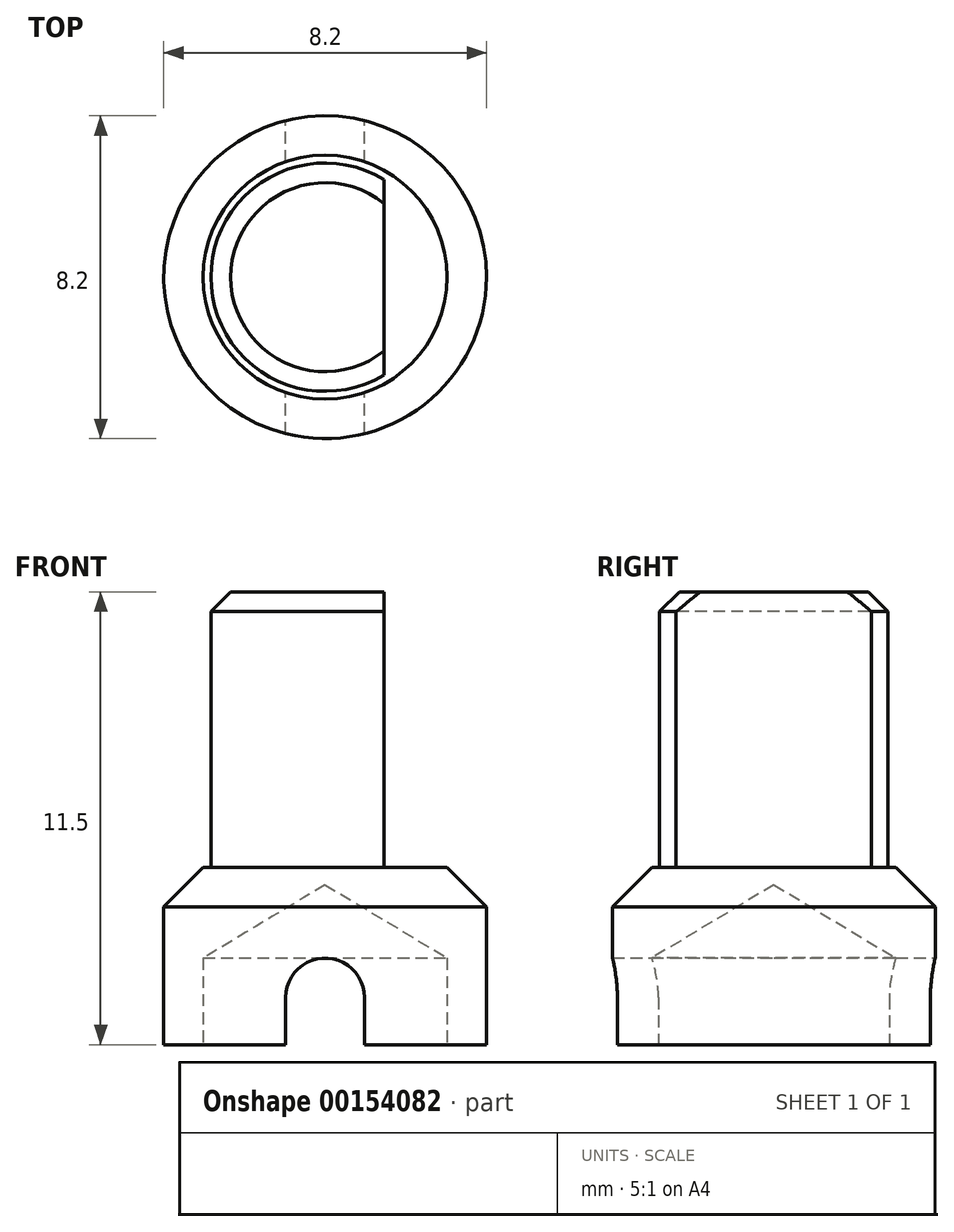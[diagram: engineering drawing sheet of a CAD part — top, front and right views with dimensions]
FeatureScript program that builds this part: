
annotation { "Feature Type Name" : "Feature", "Feature Type Description" : "" }
export const myFeature = defineFeature(function(context is Context, id is Id, definition is map)
    precondition{}
    {
        {
            var Q0;
            Q0=qCreatedBy(makeId("Top.planeOp"),FACE);
            var sketch = newSketch(context, id + "F0", { "sketchPlane" : qUnion([Q0])});
            skCircle(sketch, "E0", {"center": v(0, 0) * mm, "radius": 4.1 * mm});
            skSolve(sketch);
        }
        {
            var Q0;
            Q0=makeQuery(id+"F0.imprint","IMPRINT",FACE,{"disambiguationData":[TD([[makeQuery(id+"F0.imprint","IMPRINT",EDGE,{"derivedFrom":sQuery(id+"F0.wireOp",EDGE,"E0")}),1.0]])]});
            var Q1;
            Q1=sQuery(id+"F0.wireOp",EDGE,"E0");
            extrude(context, id + "F1", {"entities" : qUnion([Q0]), "surfaceEntities" : qUnion([Q1]), "depth" : 4.5 * mm});
        }
        {
            var Q0;
            Q0=sQuery(id+"F0.wireOp",VERTEX,"E0.center");
            var Q1;
            Q1=makeQuery(id+"F1.opExtrude","SWEPT_BODY",BODY,{"disambiguationData":[OSD([sQuery(id+"F0.wireOp",EDGE,"E0")])]});
            hole(context, id + "F2", {"style" : HoleStyle.SIMPLE, "endStyle" : HoleEndStyle.BLIND, "oppositeDirection" : true, "holeDiameter" : 6.2 * mm, "holeDepth" : 2.2 * mm, "locations" : qUnion([Q0]), "scope" : qUnion([Q1])});
        }
        {
            var Q0;
            Q0=makeQuery(id+"F1.opExtrude","CAP_FACE",FACE,{"disambiguationData":[OSD([sQuery(id+"F0.wireOp",EDGE,"E0")])],"isStart":false});
            var sketch = newSketch(context, id + "F3", { "sketchPlane" : qUnion([Q0])});
            skArc(sketch, "E1", {"start": v(1.5, 2.48) * mm, "mid": v(-2.9, 0) * mm, "end": v(1.5, -2.48) * mm});
            skLineSegment(sketch, "E2", {"start": v(1.5, 2.48) * mm, "end": v(1.5, -2.48) * mm});
            skSolve(sketch);
        }
        {
            var Q0;
            Q0=makeQuery(id+"F3.imprint","IMPRINT",FACE,{"disambiguationData":[TD([[makeQuery(id+"F3.imprint","IMPRINT",EDGE,{"derivedFrom":sQuery(id+"F3.wireOp",EDGE,"E1")}),1.0]])]});
            extrude(context, id + "F4", {"entities" : qUnion([Q0]), "operationType" : NewBodyOperationType.ADD, "depth" : 7 * mm});
        }
        {
            var Q0;
            Q0=makeQuery(id+"F4.opExtrude","CAP_EDGE",EDGE,{"disambiguationData":[OSD([sQuery(id+"F3.wireOp",EDGE,"E1")])],"isStart":false});
            chamfer(context, id + "F5", {"entities" : qUnion([Q0]), "width" : 0.5 * mm, "tangentPropagation" : true});
        }
        {
            var Q0;
            Q0=makeQuery(id+"F1.opExtrude","CAP_EDGE",EDGE,{"disambiguationData":[OSD([sQuery(id+"F0.wireOp",EDGE,"E0")])],"isStart":false});
            chamfer(context, id + "F6", {"entities" : qUnion([Q0]), "width" : 1 * mm, "tangentPropagation" : true});
        }
        {
            var Q0;
            Q0=qCreatedBy(makeId("Front.planeOp"),FACE);
            var sketch = newSketch(context, id + "F7", { "sketchPlane" : qUnion([Q0])});
            skLineSegment(sketch, "E3.bottom", {"start": v(-1, 0) * mm, "end": v(1, 0) * mm});
            skLineSegment(sketch, "E3.left", {"start": v(-1, 0) * mm, "end": v(-1, 1.2) * mm});
            skLineSegment(sketch, "E3.right", {"start": v(1, 0) * mm, "end": v(1, 1.2) * mm});
            skArc(sketch, "E4", {"start": v(-1, 1.2) * mm, "mid": v(0, 2.2) * mm, "end": v(1, 1.2) * mm});
            skSolve(sketch);
        }
        {
            var Q0;
            Q0 = qSketchRegion(id + "F7", true);
            extrude(context, id + "F8", {"entities" : qUnion([Q0]), "operationType" : NewBodyOperationType.REMOVE, "depth" : 50 * mm, "symmetric" : true});
        }
    });
